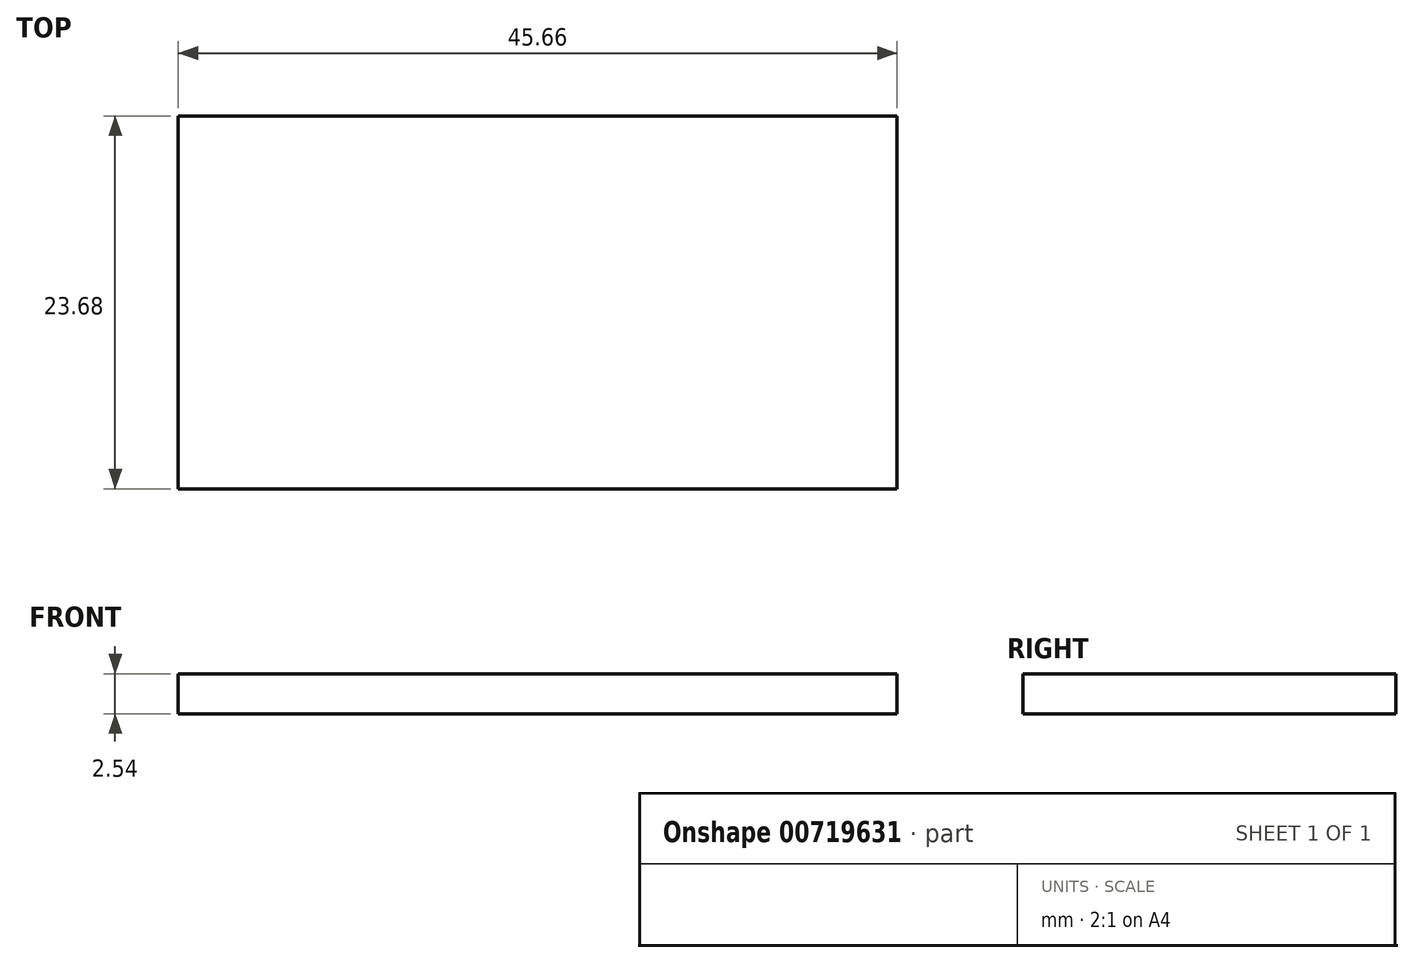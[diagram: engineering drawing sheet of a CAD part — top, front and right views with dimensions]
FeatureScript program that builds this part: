
annotation { "Feature Type Name" : "Feature", "Feature Type Description" : "" }
export const myFeature = defineFeature(function(context is Context, id is Id, definition is map)
    precondition{}
    {
        {
            var Q0;
            Q0=qCreatedBy(makeId("Top.planeOp"),FACE);
            var sketch = newSketch(context, id + "F0", { "sketchPlane" : qUnion([Q0])});
            skLineSegment(sketch, "E0.bottom", {"start": v(22.83, 11.84) * mm, "end": v(-22.83, 11.84) * mm});
            skLineSegment(sketch, "E0.top", {"start": v(22.83, -11.84) * mm, "end": v(-22.83, -11.84) * mm});
            skLineSegment(sketch, "E0.left", {"start": v(22.83, 11.84) * mm, "end": v(22.83, -11.84) * mm});
            skLineSegment(sketch, "E0.right", {"start": v(-22.83, 11.84) * mm, "end": v(-22.83, -11.84) * mm});
            skPoint(sketch, "E0.middle", {"position": v(0, 0) * mm});
            skSolve(sketch);
        }
        {
            var Q0;
            Q0=makeQuery(id+"F0.imprint","IMPRINT",FACE,{"disambiguationData":[TD([[makeQuery(id+"F0.imprint","IMPRINT",EDGE,{"derivedFrom":sQuery(id+"F0.wireOp",EDGE,"E0.bottom")}),1.0]])]});
            extrude(context, id + "F1", {"entities" : qUnion([Q0]), "depth" : 2.54 * mm, "offsetDistance" : 25.4 * mm});
        }
    });
